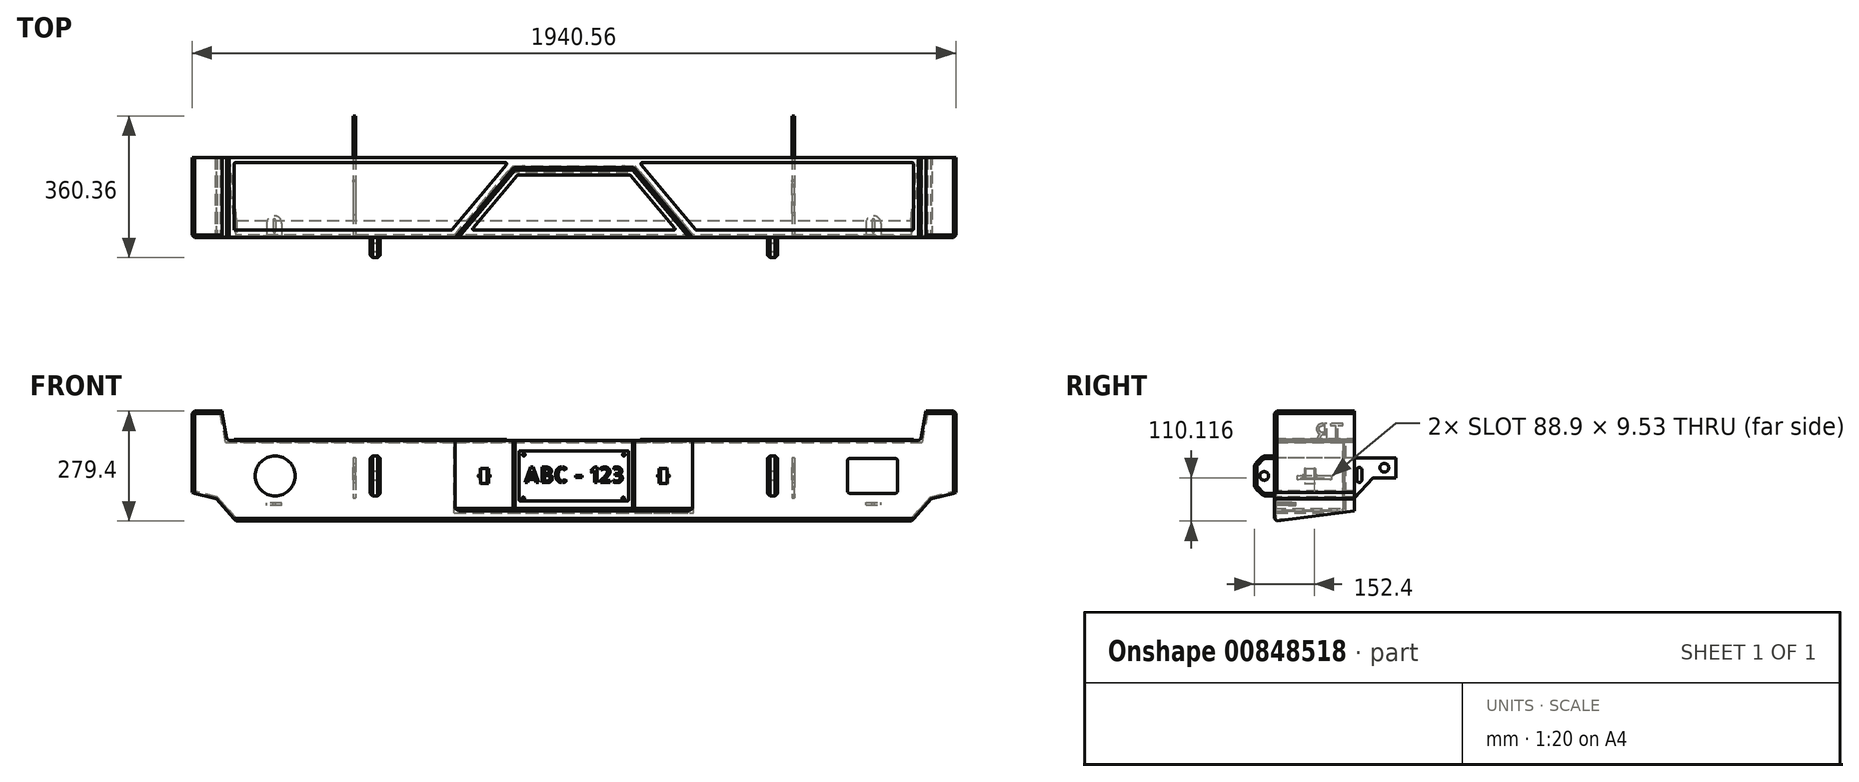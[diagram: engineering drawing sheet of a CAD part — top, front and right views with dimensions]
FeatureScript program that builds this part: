
annotation { "Feature Type Name" : "Feature", "Feature Type Description" : "" }
export const myFeature = defineFeature(function(context is Context, id is Id, definition is map)
    precondition{}
    {
        {
            var Q0;
            Q0=qCreatedBy(makeId("Top.planeOp"),FACE);
            var sketch = newSketch(context, id + "F0", { "sketchPlane" : qUnion([Q0])});
            skLineSegment(sketch, "E0.bottom", {"start": v(-970.28, -101.6) * mm, "end": v(970.28, -101.6) * mm});
            skLineSegment(sketch, "E0.top", {"start": v(-970.28, 101.6) * mm, "end": v(970.28, 101.6) * mm});
            skLineSegment(sketch, "E0.left", {"start": v(-970.28, -101.6) * mm, "end": v(-970.28, 101.6) * mm});
            skLineSegment(sketch, "E0.right", {"start": v(970.28, -101.6) * mm, "end": v(970.28, 101.6) * mm});
            skPoint(sketch, "E0.middle", {"position": v(0, 0) * mm});
            skSolve(sketch);
        }
        {
            var Q0;
            Q0=qSketchRegion(id+"F0",true);
            extrude(context, id + "F1", {"entities" : qUnion([Q0]), "depth" : 279.4 * mm, "offsetDistance" : 25.4 * mm});
        }
        {
            var Q0;
            Q0=makeQuery(id+"F1.opExtrude","SWEPT_FACE",FACE,{"disambiguationData":[OSD([sQuery(id+"F0.wireOp",EDGE,"E0.bottom")])]});
            var sketch = newSketch(context, id + "F2", { "sketchPlane" : qUnion([Q0])});
            skLineSegment(sketch, "E1", {"start": v(-970.28, 72.27) * mm, "end": v(-908.72, 57.25) * mm});
            skLineSegment(sketch, "E2", {"start": v(-908.72, 57.25) * mm, "end": v(-858.44, 0) * mm});
            skLineSegment(sketch, "E3.MirrorCS", {"start": v(908.72, 57.25) * mm, "end": v(858.44, 0) * mm});
            skLineSegment(sketch, "E4.MirrorCS", {"start": v(970.28, 72.27) * mm, "end": v(908.72, 57.25) * mm});
            skSolve(sketch);
        }
        {
            var Q0;
            {var subQ0=sQuery(id+"F2.wireOp",EDGE,"E1");Q0=makeQuery(id+"F2.imprint","IMPRINT",FACE,{"disambiguationData":[TD([[makeQuery(id+"F2.imprint","IMPRINT",EDGE,{"derivedFrom":subQ0}),-1.0]])]});}
            var Q1;
            {var subQ0=sQuery(id+"F2.wireOp",EDGE,"E3.MirrorCS");Q1=makeQuery(id+"F2.imprint","IMPRINT",FACE,{"disambiguationData":[TD([[makeQuery(id+"F2.imprint","IMPRINT",EDGE,{"derivedFrom":subQ0}),1.0]])]});}
            extrude(context, id + "F3", {"entities" : qUnion([Q0, Q1]), "operationType" : NewBodyOperationType.REMOVE, "endBound" : BoundingType.THROUGH_ALL, "oppositeDirection" : true, "depth" : 25.4 * mm});
        }
        {
            var Q0;
            Q0=makeQuery(id+"F1.opExtrude","SWEPT_FACE",FACE,{"disambiguationData":[OSD([sQuery(id+"F0.wireOp",EDGE,"E0.bottom")])]});
            var sketch = newSketch(context, id + "F4", { "sketchPlane" : qUnion([Q0])});
            skLineSegment(sketch, "E5", {"start": v(-970.28, 279.4) * mm, "end": v(-894.08, 279.4) * mm});
            skLineSegment(sketch, "E6", {"start": v(-894.08, 279.4) * mm, "end": v(-880.85, 204.36) * mm});
            skLineSegment(sketch, "E7", {"start": v(-880.85, 204.36) * mm, "end": v(880.85, 204.36) * mm});
            skLineSegment(sketch, "E8", {"start": v(880.85, 204.36) * mm, "end": v(894.08, 279.4) * mm});
            skLineSegment(sketch, "E9", {"start": v(894.08, 279.4) * mm, "end": v(970.28, 279.4) * mm});
            skSolve(sketch);
        }
        {
            var Q0;
            {var subQ0=sQuery(id+"F4.wireOp",EDGE,"E6");Q0=makeQuery(id+"F4.imprint","IMPRINT",FACE,{"disambiguationData":[TD([[makeQuery(id+"F4.imprint","IMPRINT",EDGE,{"derivedFrom":subQ0}),1.0]])]});}
            extrude(context, id + "F5", {"entities" : qUnion([Q0]), "operationType" : NewBodyOperationType.REMOVE, "endBound" : BoundingType.THROUGH_ALL, "oppositeDirection" : true, "depth" : 25.4 * mm});
        }
        {
            var Q0;
            Q0=makeQuery(id+"F5.boolean.opBoolean","COPY",FACE,{"derivedFrom":makeQuery(id+"F5.opExtrude","SWEPT_FACE",FACE,{"disambiguationData":[OSD([sQuery(id+"F4.wireOp",EDGE,"E7")])]})});
            var sketch = newSketch(context, id + "F6", { "sketchPlane" : qUnion([Q0])});
            skLineSegment(sketch, "E10", {"start": v(-301.6, -101.6) * mm, "end": v(-152.4, 76.2) * mm});
            skLineSegment(sketch, "E11", {"start": v(-152.4, 76.2) * mm, "end": v(152.4, 76.2) * mm});
            skLineSegment(sketch, "E12", {"start": v(152.4, 76.2) * mm, "end": v(301.6, -101.6) * mm});
            skSolve(sketch);
        }
        {
            var Q0;
            {var subQ0=sQuery(id+"F6.wireOp",EDGE,"E10");Q0=makeQuery(id+"F6.imprint","IMPRINT",FACE,{"disambiguationData":[TD([[makeQuery(id+"F6.imprint","IMPRINT",EDGE,{"derivedFrom":subQ0}),-1.0]])]});}
            extrude(context, id + "F7", {"entities" : qUnion([Q0]), "operationType" : NewBodyOperationType.REMOVE, "oppositeDirection" : true, "depth" : 178.96 * mm});
        }
        {
            var Q0;
            Q0=makeQuery(id+"F1.opExtrude","SWEPT_FACE",FACE,{"disambiguationData":[OSD([sQuery(id+"F0.wireOp",EDGE,"E0.bottom")])]});
            var sketch = newSketch(context, id + "F8", { "sketchPlane" : qUnion([Q0])});
            skLineSegment(sketch, "E13.bottom", {"start": v(-492.1, 165.68) * mm, "end": v(-517.5, 165.68) * mm});
            skLineSegment(sketch, "E13.top", {"start": v(-492.1, 64.08) * mm, "end": v(-517.5, 64.08) * mm});
            skLineSegment(sketch, "E13.left", {"start": v(-492.1, 165.68) * mm, "end": v(-492.1, 64.08) * mm});
            skLineSegment(sketch, "E13.right", {"start": v(-517.5, 165.68) * mm, "end": v(-517.5, 64.08) * mm});
            skPoint(sketch, "E13.middle", {"position": v(-504.8, 114.88) * mm});
            skPoint(sketch, "E13.middle.positionSnap0", {"position": v(-301.6, 114.88) * mm});
            skPoint(sketch, "E13.centerSnap0", {"position": v(-301.6, 114.88) * mm});
            skLineSegment(sketch, "E14.bottom", {"start": v(492.1, 165.68) * mm, "end": v(517.5, 165.68) * mm});
            skLineSegment(sketch, "E14.top", {"start": v(492.1, 64.08) * mm, "end": v(517.5, 64.08) * mm});
            skLineSegment(sketch, "E14.left", {"start": v(492.1, 165.68) * mm, "end": v(492.1, 64.08) * mm});
            skLineSegment(sketch, "E14.right", {"start": v(517.5, 165.68) * mm, "end": v(517.5, 64.08) * mm});
            skPoint(sketch, "E14.middle", {"position": v(504.8, 114.88) * mm});
            skPoint(sketch, "E14.middle.positionSnap0", {"position": v(301.6, 114.88) * mm});
            skPoint(sketch, "E14.centerSnap0", {"position": v(301.6, 114.88) * mm});
            skSolve(sketch);
        }
        {
            var Q0;
            Q0=qSketchRegion(id+"F8",true);
            extrude(context, id + "F9", {"entities" : qUnion([Q0]), "depth" : 50.8 * mm});
        }
        {
            var Q0;
            Q0=makeQuery(id+"F9.opExtrude","SWEPT_FACE",FACE,{"disambiguationData":[OSD([sQuery(id+"F8.wireOp",EDGE,"E13.right")])]});
            var sketch = newSketch(context, id + "F10", { "sketchPlane" : qUnion([Q0])});
            skCircle(sketch, "E15", {"center": v(127, 114.88) * mm, "radius": 11.11 * mm});
            skPoint(sketch, "E15.centerSnap0", {"position": v(127, 165.68) * mm});
            skPoint(sketch, "E15.centerSnap1", {"position": v(152.4, 114.88) * mm});
            skSolve(sketch);
        }
        {
            var Q0;
            Q0=qSketchRegion(id+"F10",true);
            extrude(context, id + "F11", {"entities" : qUnion([Q0]), "operationType" : NewBodyOperationType.REMOVE, "endBound" : BoundingType.THROUGH_ALL, "oppositeDirection" : true, "depth" : 25.4 * mm});
        }
        {
            var Q0;
            Q0=makeQuery(id+"F9.opExtrude","CAP_EDGE",EDGE,{"disambiguationData":[OSD([sQuery(id+"F8.wireOp",EDGE,"E13.bottom")])],"isStart":false});
            var Q1;
            Q1=makeQuery(id+"F9.opExtrude","CAP_EDGE",EDGE,{"disambiguationData":[OSD([sQuery(id+"F8.wireOp",EDGE,"E13.top")])],"isStart":false});
            var Q2;
            Q2=makeQuery(id+"F9.opExtrude","CAP_EDGE",EDGE,{"disambiguationData":[OSD([sQuery(id+"F8.wireOp",EDGE,"E14.bottom")])],"isStart":false});
            var Q3;
            Q3=makeQuery(id+"F9.opExtrude","CAP_EDGE",EDGE,{"disambiguationData":[OSD([sQuery(id+"F8.wireOp",EDGE,"E14.top")])],"isStart":false});
            chamfer(context, id + "F12", {"entities" : qUnion([Q0, Q1, Q2, Q3]), "width" : 22.22 * mm, "tangentPropagation" : true});
        }
        {
            var Q0;
            {var subQ0=sQuery(id+"F8.wireOp",EDGE,"E13.bottom");Q0=makeQuery(id+"F12.opChamfer","BLEND_EDGE",EDGE,{"blendedFrom":[makeQuery(id+"F9.opExtrude","CAP_EDGE",EDGE,{"disambiguationData":[OSD([subQ0])],"isStart":false}),makeQuery(id+"F9.opExtrude","SWEPT_FACE",FACE,{"disambiguationData":[OSD([subQ0])]})],"blendedInto":[makeQuery(id+"F9.opExtrude","SWEPT_FACE",FACE,{"disambiguationData":[OSD([subQ0])]})]});}
            var Q1;
            {var subQ0=sQuery(id+"F8.wireOp",EDGE,"E13.bottom");Q1=makeQuery(id+"F12.opChamfer","BLEND_EDGE",EDGE,{"blendedFrom":[makeQuery(id+"F9.opExtrude","CAP_EDGE",EDGE,{"disambiguationData":[OSD([subQ0])],"isStart":false}),makeQuery(id+"F9.opExtrude","CAP_FACE",FACE,{"disambiguationData":[OSD([subQ0,sQuery(id+"F8.wireOp",EDGE,"E13.top"),sQuery(id+"F8.wireOp",EDGE,"E13.left"),sQuery(id+"F8.wireOp",EDGE,"E13.right")])],"isStart":false})],"blendedInto":[makeQuery(id+"F9.opExtrude","CAP_FACE",FACE,{"disambiguationData":[OSD([subQ0,sQuery(id+"F8.wireOp",EDGE,"E13.top"),sQuery(id+"F8.wireOp",EDGE,"E13.left"),sQuery(id+"F8.wireOp",EDGE,"E13.right")])],"isStart":false})]});}
            var Q2;
            {var subQ0=sQuery(id+"F8.wireOp",EDGE,"E13.top");Q2=makeQuery(id+"F12.opChamfer","BLEND_EDGE",EDGE,{"blendedFrom":[makeQuery(id+"F9.opExtrude","CAP_EDGE",EDGE,{"disambiguationData":[OSD([subQ0])],"isStart":false}),makeQuery(id+"F9.opExtrude","CAP_FACE",FACE,{"disambiguationData":[OSD([sQuery(id+"F8.wireOp",EDGE,"E13.bottom"),subQ0,sQuery(id+"F8.wireOp",EDGE,"E13.left"),sQuery(id+"F8.wireOp",EDGE,"E13.right")])],"isStart":false})],"blendedInto":[makeQuery(id+"F9.opExtrude","CAP_FACE",FACE,{"disambiguationData":[OSD([sQuery(id+"F8.wireOp",EDGE,"E13.bottom"),subQ0,sQuery(id+"F8.wireOp",EDGE,"E13.left"),sQuery(id+"F8.wireOp",EDGE,"E13.right")])],"isStart":false})]});}
            var Q3;
            {var subQ0=sQuery(id+"F8.wireOp",EDGE,"E13.top");Q3=makeQuery(id+"F12.opChamfer","BLEND_EDGE",EDGE,{"blendedFrom":[makeQuery(id+"F9.opExtrude","CAP_EDGE",EDGE,{"disambiguationData":[OSD([subQ0])],"isStart":false}),makeQuery(id+"F9.opExtrude","SWEPT_FACE",FACE,{"disambiguationData":[OSD([subQ0])]})],"blendedInto":[makeQuery(id+"F9.opExtrude","SWEPT_FACE",FACE,{"disambiguationData":[OSD([subQ0])]})]});}
            var Q4;
            {var subQ0=sQuery(id+"F8.wireOp",EDGE,"E14.bottom");Q4=makeQuery(id+"F12.opChamfer","BLEND_EDGE",EDGE,{"blendedFrom":[makeQuery(id+"F9.opExtrude","CAP_EDGE",EDGE,{"disambiguationData":[OSD([subQ0])],"isStart":false}),makeQuery(id+"F9.opExtrude","SWEPT_FACE",FACE,{"disambiguationData":[OSD([subQ0])]})],"blendedInto":[makeQuery(id+"F9.opExtrude","SWEPT_FACE",FACE,{"disambiguationData":[OSD([subQ0])]})]});}
            var Q5;
            {var subQ0=sQuery(id+"F8.wireOp",EDGE,"E14.bottom");Q5=makeQuery(id+"F12.opChamfer","BLEND_EDGE",EDGE,{"blendedFrom":[makeQuery(id+"F9.opExtrude","CAP_EDGE",EDGE,{"disambiguationData":[OSD([subQ0])],"isStart":false}),makeQuery(id+"F9.opExtrude","CAP_FACE",FACE,{"disambiguationData":[OSD([subQ0,sQuery(id+"F8.wireOp",EDGE,"E14.top"),sQuery(id+"F8.wireOp",EDGE,"E14.left"),sQuery(id+"F8.wireOp",EDGE,"E14.right")])],"isStart":false})],"blendedInto":[makeQuery(id+"F9.opExtrude","CAP_FACE",FACE,{"disambiguationData":[OSD([subQ0,sQuery(id+"F8.wireOp",EDGE,"E14.top"),sQuery(id+"F8.wireOp",EDGE,"E14.left"),sQuery(id+"F8.wireOp",EDGE,"E14.right")])],"isStart":false})]});}
            var Q6;
            {var subQ0=sQuery(id+"F8.wireOp",EDGE,"E14.top");Q6=makeQuery(id+"F12.opChamfer","BLEND_EDGE",EDGE,{"blendedFrom":[makeQuery(id+"F9.opExtrude","CAP_EDGE",EDGE,{"disambiguationData":[OSD([subQ0])],"isStart":false}),makeQuery(id+"F9.opExtrude","CAP_FACE",FACE,{"disambiguationData":[OSD([sQuery(id+"F8.wireOp",EDGE,"E14.bottom"),subQ0,sQuery(id+"F8.wireOp",EDGE,"E14.left"),sQuery(id+"F8.wireOp",EDGE,"E14.right")])],"isStart":false})],"blendedInto":[makeQuery(id+"F9.opExtrude","CAP_FACE",FACE,{"disambiguationData":[OSD([sQuery(id+"F8.wireOp",EDGE,"E14.bottom"),subQ0,sQuery(id+"F8.wireOp",EDGE,"E14.left"),sQuery(id+"F8.wireOp",EDGE,"E14.right")])],"isStart":false})]});}
            var Q7;
            {var subQ0=sQuery(id+"F8.wireOp",EDGE,"E14.top");Q7=makeQuery(id+"F12.opChamfer","BLEND_EDGE",EDGE,{"blendedFrom":[makeQuery(id+"F9.opExtrude","CAP_EDGE",EDGE,{"disambiguationData":[OSD([subQ0])],"isStart":false}),makeQuery(id+"F9.opExtrude","SWEPT_FACE",FACE,{"disambiguationData":[OSD([subQ0])]})],"blendedInto":[makeQuery(id+"F9.opExtrude","SWEPT_FACE",FACE,{"disambiguationData":[OSD([subQ0])]})]});}
            fillet(context, id + "F13", {"entities" : qUnion([Q0, Q1, Q2, Q3, Q4, Q5, Q6, Q7]), "radius" : 19.05 * mm, "tangentPropagation" : true, "allowEdgeOverflow" : false});
        }
        {
            var Q0;
            Q0=makeQuery(id+"F9.opExtrude","SWEPT_EDGE",EDGE,{"disambiguationData":[OSD([sQuery(id+"F8.wireOp",EDGE,"E13.bottom"),sQuery(id+"F8.wireOp",EDGE,"E13.right")])]});
            var Q1;
            Q1=makeQuery(id+"F9.opExtrude","SWEPT_EDGE",EDGE,{"disambiguationData":[OSD([sQuery(id+"F8.wireOp",EDGE,"E13.bottom"),sQuery(id+"F8.wireOp",EDGE,"E13.left")])]});
            var Q2;
            Q2=makeQuery(id+"F9.opExtrude","SWEPT_EDGE",EDGE,{"disambiguationData":[OSD([sQuery(id+"F8.wireOp",EDGE,"E14.bottom"),sQuery(id+"F8.wireOp",EDGE,"E14.left")])]});
            var Q3;
            Q3=makeQuery(id+"F9.opExtrude","SWEPT_EDGE",EDGE,{"disambiguationData":[OSD([sQuery(id+"F8.wireOp",EDGE,"E14.bottom"),sQuery(id+"F8.wireOp",EDGE,"E14.right")])]});
            chamfer(context, id + "F14", {"entities" : qUnion([Q0, Q1, Q2, Q3]), "width" : 6.35 * mm, "tangentPropagation" : true});
        }
        {
            var Q0;
            Q0=makeQuery(id+"F1.opExtrude","SWEPT_FACE",FACE,{"disambiguationData":[OSD([sQuery(id+"F0.wireOp",EDGE,"E0.top")])]});
            shell(context, id + "F15", {"entities" : qUnion([Q0]), "thickness" : 4.76 * mm});
        }
        {
            var Q0;
            Q0=makeQuery(id+"F1.opExtrude","SWEPT_FACE",FACE,{"disambiguationData":[OSD([sQuery(id+"F0.wireOp",EDGE,"E0.bottom")])]});
            var sketch = newSketch(context, id + "F16", { "sketchPlane" : qUnion([Q0])});
            skCircle(sketch, "E16", {"center": v(-758.8, 114.88) * mm, "radius": 50.8 * mm});
            skPoint(sketch, "E16.centerSnap0", {"position": v(-301.6, 114.88) * mm});
            skPoint(sketch, "E17.centerSnap0", {"position": v(301.6, 114.88) * mm});
            skLineSegment(sketch, "E18.bottom", {"start": v(695.3, 70.43) * mm, "end": v(822.3, 70.43) * mm});
            skLineSegment(sketch, "E18.top", {"start": v(695.3, 159.33) * mm, "end": v(822.3, 159.33) * mm});
            skLineSegment(sketch, "E18.left", {"start": v(695.3, 70.43) * mm, "end": v(695.3, 159.33) * mm});
            skLineSegment(sketch, "E18.right", {"start": v(822.3, 70.43) * mm, "end": v(822.3, 159.33) * mm});
            skPoint(sketch, "E18.middle", {"position": v(758.8, 114.88) * mm});
            skSolve(sketch);
        }
        {
            var Q0;
            Q0=qSketchRegion(id+"F16",true);
            extrude(context, id + "F17", {"entities" : qUnion([Q0]), "operationType" : NewBodyOperationType.REMOVE, "endBound" : BoundingType.THROUGH_ALL, "oppositeDirection" : true, "depth" : 25.4 * mm});
        }
        {
            var Q0;
            Q0=makeQuery(id+"F1.opExtrude","CAP_EDGE",EDGE,{"disambiguationData":[OSD([sQuery(id+"F0.wireOp",EDGE,"E0.bottom")])],"isStart":true});
            var Q1;
            Q1=makeQuery(id+"F3.boolean.opBoolean","COPY",EDGE,{"derivedFrom":makeQuery(id+"F3.opExtrude","CAP_EDGE",EDGE,{"disambiguationData":[OSD([sQuery(id+"F2.wireOp",EDGE,"E2")])],"isStart":true})});
            var Q2;
            Q2=makeQuery(id+"F3.boolean.opBoolean","COPY",EDGE,{"derivedFrom":makeQuery(id+"F3.opExtrude","CAP_EDGE",EDGE,{"disambiguationData":[OSD([sQuery(id+"F2.wireOp",EDGE,"E1")])],"isStart":true})});
            var Q3;
            Q3=makeQuery(id+"F3.boolean.opBoolean","COPY",EDGE,{"derivedFrom":makeQuery(id+"F3.opExtrude","CAP_EDGE",EDGE,{"disambiguationData":[OSD([sQuery(id+"F2.wireOp",EDGE,"E3.MirrorCS")])],"isStart":true})});
            var Q4;
            Q4=makeQuery(id+"F3.boolean.opBoolean","COPY",EDGE,{"derivedFrom":makeQuery(id+"F3.opExtrude","CAP_EDGE",EDGE,{"disambiguationData":[OSD([sQuery(id+"F2.wireOp",EDGE,"E4.MirrorCS")])],"isStart":true})});
            var Q5;
            Q5=makeQuery(id+"F1.opExtrude","SWEPT_EDGE",EDGE,{"disambiguationData":[OSD([sQuery(id+"F0.wireOp",EDGE,"E0.bottom"),sQuery(id+"F0.wireOp",EDGE,"E0.right")])]});
            var Q6;
            Q6=makeQuery(id+"F1.opExtrude","SWEPT_EDGE",EDGE,{"disambiguationData":[OSD([sQuery(id+"F0.wireOp",EDGE,"E0.bottom"),sQuery(id+"F0.wireOp",EDGE,"E0.left")])]});
            var Q7;
            Q7=makeQuery(id+"F3.boolean.opBoolean","COPY",EDGE,{"derivedFrom":makeQuery(id+"F3.opExtrude","SWEPT_EDGE",EDGE,{"disambiguationData":[OSD([sQuery(id+"F0.wireOp",EDGE,"E0.bottom"),sQuery(id+"F0.wireOp",EDGE,"E0.left"),sQuery(id+"F2.wireOp",EDGE,"E1")])]})});
            var Q8;
            Q8=makeQuery(id+"F3.boolean.opBoolean","COPY",EDGE,{"derivedFrom":makeQuery(id+"F3.opExtrude","SWEPT_EDGE",EDGE,{"disambiguationData":[OSD([sQuery(id+"F2.wireOp",EDGE,"E1"),sQuery(id+"F2.wireOp",EDGE,"E2")])]})});
            var Q9;
            Q9=makeQuery(id+"F3.boolean.opBoolean","COPY",EDGE,{"derivedFrom":makeQuery(id+"F3.opExtrude","SWEPT_EDGE",EDGE,{"disambiguationData":[OSD([sQuery(id+"F0.wireOp",EDGE,"E0.bottom"),sQuery(id+"F2.wireOp",EDGE,"E2")])]})});
            var Q10;
            Q10=makeQuery(id+"F3.boolean.opBoolean","COPY",EDGE,{"derivedFrom":makeQuery(id+"F3.opExtrude","SWEPT_EDGE",EDGE,{"disambiguationData":[OSD([sQuery(id+"F0.wireOp",EDGE,"E0.bottom"),sQuery(id+"F2.wireOp",EDGE,"E3.MirrorCS")])]})});
            var Q11;
            Q11=makeQuery(id+"F3.boolean.opBoolean","COPY",EDGE,{"derivedFrom":makeQuery(id+"F3.opExtrude","SWEPT_EDGE",EDGE,{"disambiguationData":[OSD([sQuery(id+"F2.wireOp",EDGE,"E3.MirrorCS"),sQuery(id+"F2.wireOp",EDGE,"E4.MirrorCS")])]})});
            var Q12;
            Q12=makeQuery(id+"F3.boolean.opBoolean","COPY",EDGE,{"derivedFrom":makeQuery(id+"F3.opExtrude","SWEPT_EDGE",EDGE,{"disambiguationData":[OSD([sQuery(id+"F0.wireOp",EDGE,"E0.bottom"),sQuery(id+"F0.wireOp",EDGE,"E0.right"),sQuery(id+"F2.wireOp",EDGE,"E4.MirrorCS")])]})});
            var Q13;
            Q13=makeQuery(id+"F1.opExtrude","CAP_EDGE",EDGE,{"disambiguationData":[OSD([sQuery(id+"F0.wireOp",EDGE,"E0.left")])],"isStart":false});
            var Q14;
            Q14=makeQuery(id+"F1.opExtrude","CAP_EDGE",EDGE,{"disambiguationData":[OSD([sQuery(id+"F0.wireOp",EDGE,"E0.right")])],"isStart":false});
            var Q15;
            {var subQ0=sQuery(id+"F0.wireOp",EDGE,"E0.bottom");var subQ1=sQuery(id+"F0.wireOp",EDGE,"E0.right");Q15=makeQuery(id+"F5.boolean.opBoolean","SPLIT",EDGE,{"disambiguationData":[TD([makeQuery(id+"F1.opExtrude","SWEPT_FACE",FACE,{"disambiguationData":[OSD([subQ1])]})])],"derivedFrom":makeQuery(id+"F1.opExtrude","CAP_EDGE",EDGE,{"disambiguationData":[OSD([subQ0])],"isStart":false})});}
            var Q16;
            Q16=makeQuery(id+"F5.boolean.opBoolean","COPY",EDGE,{"derivedFrom":makeQuery(id+"F5.opExtrude","CAP_EDGE",EDGE,{"disambiguationData":[OSD([sQuery(id+"F4.wireOp",EDGE,"E8")])],"isStart":true})});
            var Q17;
            {var subQ0=sQuery(id+"F4.wireOp",EDGE,"E7");Q17=makeQuery(id+"F7.boolean.opBoolean","SPLIT",EDGE,{"disambiguationData":[TD([makeQuery(id+"F5.boolean.opBoolean","COPY",FACE,{"derivedFrom":makeQuery(id+"F5.opExtrude","SWEPT_FACE",FACE,{"disambiguationData":[OSD([sQuery(id+"F4.wireOp",EDGE,"E8")])]})})])],"derivedFrom":makeQuery(id+"F5.boolean.opBoolean","COPY",EDGE,{"derivedFrom":makeQuery(id+"F5.opExtrude","CAP_EDGE",EDGE,{"disambiguationData":[OSD([subQ0])],"isStart":true})})});}
            var Q18;
            {var subQ0=sQuery(id+"F4.wireOp",EDGE,"E7");Q18=makeQuery(id+"F7.boolean.opBoolean","SPLIT",EDGE,{"disambiguationData":[TD([makeQuery(id+"F5.boolean.opBoolean","COPY",FACE,{"derivedFrom":makeQuery(id+"F5.opExtrude","SWEPT_FACE",FACE,{"disambiguationData":[OSD([sQuery(id+"F4.wireOp",EDGE,"E6")])]})})])],"derivedFrom":makeQuery(id+"F5.boolean.opBoolean","COPY",EDGE,{"derivedFrom":makeQuery(id+"F5.opExtrude","CAP_EDGE",EDGE,{"disambiguationData":[OSD([subQ0])],"isStart":true})})});}
            var Q19;
            {var subQ0=sQuery(id+"F0.wireOp",EDGE,"E0.bottom");var subQ1=sQuery(id+"F0.wireOp",EDGE,"E0.left");Q19=makeQuery(id+"F5.boolean.opBoolean","SPLIT",EDGE,{"disambiguationData":[TD([makeQuery(id+"F1.opExtrude","SWEPT_FACE",FACE,{"disambiguationData":[OSD([subQ1])]})])],"derivedFrom":makeQuery(id+"F1.opExtrude","CAP_EDGE",EDGE,{"disambiguationData":[OSD([subQ0])],"isStart":false})});}
            var Q20;
            Q20=makeQuery(id+"F5.boolean.opBoolean","COPY",EDGE,{"derivedFrom":makeQuery(id+"F5.opExtrude","CAP_EDGE",EDGE,{"disambiguationData":[OSD([sQuery(id+"F4.wireOp",EDGE,"E6")])],"isStart":true})});
            var Q21;
            Q21=makeQuery(id+"F5.boolean.opBoolean","COPY",EDGE,{"derivedFrom":makeQuery(id+"F5.opExtrude","SWEPT_EDGE",EDGE,{"disambiguationData":[OSD([sQuery(id+"F0.wireOp",EDGE,"E0.bottom"),sQuery(id+"F4.wireOp",EDGE,"E5"),sQuery(id+"F4.wireOp",EDGE,"E6")])]})});
            var Q22;
            Q22=makeQuery(id+"F5.boolean.opBoolean","COPY",EDGE,{"derivedFrom":makeQuery(id+"F5.opExtrude","SWEPT_EDGE",EDGE,{"disambiguationData":[OSD([sQuery(id+"F0.wireOp",EDGE,"E0.bottom"),sQuery(id+"F4.wireOp",EDGE,"E8"),sQuery(id+"F4.wireOp",EDGE,"E9")])]})});
            var Q23;
            Q23=makeQuery(id+"F5.boolean.opBoolean","COPY",EDGE,{"derivedFrom":makeQuery(id+"F5.opExtrude","SWEPT_EDGE",EDGE,{"disambiguationData":[OSD([sQuery(id+"F4.wireOp",EDGE,"E7"),sQuery(id+"F4.wireOp",EDGE,"E8")])]})});
            var Q24;
            Q24=makeQuery(id+"F5.boolean.opBoolean","COPY",EDGE,{"derivedFrom":makeQuery(id+"F5.opExtrude","SWEPT_EDGE",EDGE,{"disambiguationData":[OSD([sQuery(id+"F4.wireOp",EDGE,"E6"),sQuery(id+"F4.wireOp",EDGE,"E7")])]})});
            var Q25;
            Q25=makeQuery(id+"F7.boolean.opBoolean","COPY",EDGE,{"derivedFrom":makeQuery(id+"F7.opExtrude","CAP_EDGE",EDGE,{"disambiguationData":[OSD([sQuery(id+"F6.wireOp",EDGE,"E10")])],"isStart":true})});
            var Q26;
            Q26=makeQuery(id+"F7.boolean.opBoolean","COPY",EDGE,{"derivedFrom":makeQuery(id+"F7.opExtrude","SWEPT_EDGE",EDGE,{"disambiguationData":[OSD([sQuery(id+"F4.wireOp",EDGE,"E7"),sQuery(id+"F6.wireOp",EDGE,"E10")])]})});
            var Q27;
            Q27=makeQuery(id+"F7.boolean.opBoolean","COPY",EDGE,{"derivedFrom":makeQuery(id+"F7.opExtrude","CAP_EDGE",EDGE,{"disambiguationData":[OSD([sQuery(id+"F4.wireOp",EDGE,"E7")])],"isStart":false})});
            var Q28;
            Q28=makeQuery(id+"F7.boolean.opBoolean","COPY",EDGE,{"derivedFrom":makeQuery(id+"F7.opExtrude","SWEPT_EDGE",EDGE,{"disambiguationData":[OSD([sQuery(id+"F4.wireOp",EDGE,"E7"),sQuery(id+"F6.wireOp",EDGE,"E12")])]})});
            var Q29;
            Q29=makeQuery(id+"F7.boolean.opBoolean","COPY",EDGE,{"derivedFrom":makeQuery(id+"F7.opExtrude","CAP_EDGE",EDGE,{"disambiguationData":[OSD([sQuery(id+"F6.wireOp",EDGE,"E12")])],"isStart":true})});
            var Q30;
            Q30=makeQuery(id+"F7.boolean.opBoolean","COPY",EDGE,{"derivedFrom":makeQuery(id+"F7.opExtrude","CAP_EDGE",EDGE,{"disambiguationData":[OSD([sQuery(id+"F6.wireOp",EDGE,"E11")])],"isStart":true})});
            var Q31;
            Q31=makeQuery(id+"F7.boolean.opBoolean","COPY",EDGE,{"derivedFrom":makeQuery(id+"F7.opExtrude","SWEPT_EDGE",EDGE,{"disambiguationData":[OSD([sQuery(id+"F6.wireOp",EDGE,"E11"),sQuery(id+"F6.wireOp",EDGE,"E12")])]})});
            var Q32;
            Q32=makeQuery(id+"F7.boolean.opBoolean","COPY",EDGE,{"derivedFrom":makeQuery(id+"F7.opExtrude","SWEPT_EDGE",EDGE,{"disambiguationData":[OSD([sQuery(id+"F6.wireOp",EDGE,"E10"),sQuery(id+"F6.wireOp",EDGE,"E11")])]})});
            var Q33;
            Q33=makeQuery(id+"F7.boolean.opBoolean","COPY",EDGE,{"derivedFrom":makeQuery(id+"F7.opExtrude","CAP_EDGE",EDGE,{"disambiguationData":[OSD([sQuery(id+"F6.wireOp",EDGE,"E10")])],"isStart":false})});
            var Q34;
            Q34=makeQuery(id+"F7.boolean.opBoolean","COPY",EDGE,{"derivedFrom":makeQuery(id+"F7.opExtrude","CAP_EDGE",EDGE,{"disambiguationData":[OSD([sQuery(id+"F6.wireOp",EDGE,"E11")])],"isStart":false})});
            var Q35;
            Q35=makeQuery(id+"F7.boolean.opBoolean","COPY",EDGE,{"derivedFrom":makeQuery(id+"F7.opExtrude","CAP_EDGE",EDGE,{"disambiguationData":[OSD([sQuery(id+"F6.wireOp",EDGE,"E12")])],"isStart":false})});
            chamfer(context, id + "F18", {"entities" : qUnion([Q0, Q1, Q2, Q3, Q4, Q5, Q6, Q7, Q8, Q9, Q10, Q11, Q12, Q13, Q14, Q15, Q16, Q17, Q18, Q19, Q20, Q21, Q22, Q23, Q24, Q25, Q26, Q27, Q28, Q29, Q30, Q31, Q32, Q33, Q34, Q35]), "width" : 6.35 * mm, "tangentPropagation" : true});
        }
        {
            var Q0;
            Q0=makeQuery(id+"F15.opShell","OFFSET_FACE",FACE,{"disambiguationData":[OSD([sQuery(id+"F0.wireOp",EDGE,"E0.bottom")])]});
            var sketch = newSketch(context, id + "F19", { "sketchPlane" : qUnion([Q0])});
            skLineSegment(sketch, "E19.bottom", {"start": v(-741.96, 40.86) * mm, "end": v(-780.06, 40.86) * mm});
            skLineSegment(sketch, "E19.top", {"start": v(-741.96, 47.2) * mm, "end": v(-780.06, 47.2) * mm});
            skLineSegment(sketch, "E19.left", {"start": v(-741.96, 40.86) * mm, "end": v(-741.96, 47.2) * mm});
            skLineSegment(sketch, "E19.right", {"start": v(-780.06, 40.86) * mm, "end": v(-780.06, 47.2) * mm});
            skPoint(sketch, "E19.middle", {"position": v(-761.01, 44.03) * mm});
            skLineSegment(sketch, "E20.bottom", {"start": v(741.96, 40.36) * mm, "end": v(780.06, 40.36) * mm});
            skLineSegment(sketch, "E20.top", {"start": v(741.96, 46.71) * mm, "end": v(780.06, 46.71) * mm});
            skLineSegment(sketch, "E20.left", {"start": v(741.96, 40.36) * mm, "end": v(741.96, 46.71) * mm});
            skLineSegment(sketch, "E20.right", {"start": v(780.06, 40.36) * mm, "end": v(780.06, 46.71) * mm});
            skPoint(sketch, "E20.middle", {"position": v(761.01, 43.54) * mm});
            skSolve(sketch);
        }
        {
            var Q0;
            Q0=qSketchRegion(id+"F19",true);
            extrude(context, id + "F20", {"entities" : qUnion([Q0]), "depth" : 50.8 * mm});
        }
        {
            var Q0;
            Q0=makeQuery(id+"F20.opExtrude","SWEPT_FACE",FACE,{"disambiguationData":[OSD([sQuery(id+"F19.wireOp",EDGE,"E19.top")])]});
            var sketch = newSketch(context, id + "F21", { "sketchPlane" : qUnion([Q0])});
            skLineSegment(sketch, "E21.bottom", {"start": v(757.84, -53.98) * mm, "end": v(764.19, -53.98) * mm});
            skLineSegment(sketch, "E21.top", {"start": v(757.84, -88.9) * mm, "end": v(764.19, -88.9) * mm});
            skLineSegment(sketch, "E21.left", {"start": v(757.84, -53.98) * mm, "end": v(757.84, -88.9) * mm});
            skLineSegment(sketch, "E21.right", {"start": v(764.19, -53.98) * mm, "end": v(764.19, -88.9) * mm});
            skPoint(sketch, "E21.middle", {"position": v(761.01, -71.44) * mm});
            skPoint(sketch, "E21.middle.positionSnap0", {"position": v(761.01, -96.84) * mm});
            skPoint(sketch, "E21.middle.positionSnap1", {"position": v(741.96, -71.44) * mm});
            skPoint(sketch, "E21.centerSnap0", {"position": v(761.01, -96.84) * mm});
            skPoint(sketch, "E21.centerSnap1", {"position": v(741.96, -71.44) * mm});
            skSolve(sketch);
        }
        {
            var Q0;
            Q0=qSketchRegion(id+"F21",true);
            extrude(context, id + "F22", {"entities" : qUnion([Q0]), "operationType" : NewBodyOperationType.REMOVE, "oppositeDirection" : true, "depth" : 6.35 * mm});
        }
        {
            var Q0;
            Q0=makeQuery(id+"F20.opExtrude","SWEPT_FACE",FACE,{"disambiguationData":[OSD([sQuery(id+"F19.wireOp",EDGE,"E20.top")])]});
            var sketch = newSketch(context, id + "F23", { "sketchPlane" : qUnion([Q0])});
            skLineSegment(sketch, "E22.bottom", {"start": v(-764.19, -53.98) * mm, "end": v(-757.84, -53.98) * mm});
            skLineSegment(sketch, "E22.top", {"start": v(-764.19, -88.9) * mm, "end": v(-757.84, -88.9) * mm});
            skLineSegment(sketch, "E22.left", {"start": v(-764.19, -53.98) * mm, "end": v(-764.19, -88.9) * mm});
            skLineSegment(sketch, "E22.right", {"start": v(-757.84, -53.98) * mm, "end": v(-757.84, -88.9) * mm});
            skPoint(sketch, "E22.middle", {"position": v(-761.01, -71.44) * mm});
            skPoint(sketch, "E22.middle.positionSnap0", {"position": v(-741.96, -71.44) * mm});
            skPoint(sketch, "E22.middle.positionSnap1", {"position": v(-761.01, -46.04) * mm});
            skPoint(sketch, "E22.centerSnap0", {"position": v(-741.96, -71.44) * mm});
            skPoint(sketch, "E22.centerSnap1", {"position": v(-761.01, -46.04) * mm});
            skSolve(sketch);
        }
        {
            var Q0;
            Q0=qSketchRegion(id+"F23",true);
            extrude(context, id + "F24", {"entities" : qUnion([Q0]), "operationType" : NewBodyOperationType.REMOVE, "oppositeDirection" : true, "depth" : 6.35 * mm});
        }
        {
            var Q0;
            Q0=makeQuery(id+"F22.boolean.opBoolean","COPY",EDGE,{"derivedFrom":makeQuery(id+"F22.opExtrude","SWEPT_EDGE",EDGE,{"disambiguationData":[OSD([sQuery(id+"F21.wireOp",EDGE,"E21.top"),sQuery(id+"F21.wireOp",EDGE,"E21.left")])]})});
            var Q1;
            Q1=makeQuery(id+"F22.boolean.opBoolean","COPY",EDGE,{"derivedFrom":makeQuery(id+"F22.opExtrude","SWEPT_EDGE",EDGE,{"disambiguationData":[OSD([sQuery(id+"F21.wireOp",EDGE,"E21.top"),sQuery(id+"F21.wireOp",EDGE,"E21.right")])]})});
            var Q2;
            Q2=makeQuery(id+"F22.boolean.opBoolean","COPY",EDGE,{"derivedFrom":makeQuery(id+"F22.opExtrude","SWEPT_EDGE",EDGE,{"disambiguationData":[OSD([sQuery(id+"F21.wireOp",EDGE,"E21.bottom"),sQuery(id+"F21.wireOp",EDGE,"E21.right")])]})});
            var Q3;
            Q3=makeQuery(id+"F22.boolean.opBoolean","COPY",EDGE,{"derivedFrom":makeQuery(id+"F22.opExtrude","SWEPT_EDGE",EDGE,{"disambiguationData":[OSD([sQuery(id+"F21.wireOp",EDGE,"E21.bottom"),sQuery(id+"F21.wireOp",EDGE,"E21.left")])]})});
            var Q4;
            Q4=makeQuery(id+"F24.boolean.opBoolean","COPY",EDGE,{"derivedFrom":makeQuery(id+"F24.opExtrude","SWEPT_EDGE",EDGE,{"disambiguationData":[OSD([sQuery(id+"F23.wireOp",EDGE,"E22.bottom"),sQuery(id+"F23.wireOp",EDGE,"E22.left")])]})});
            var Q5;
            Q5=makeQuery(id+"F24.boolean.opBoolean","COPY",EDGE,{"derivedFrom":makeQuery(id+"F24.opExtrude","SWEPT_EDGE",EDGE,{"disambiguationData":[OSD([sQuery(id+"F23.wireOp",EDGE,"E22.bottom"),sQuery(id+"F23.wireOp",EDGE,"E22.right")])]})});
            var Q6;
            Q6=makeQuery(id+"F24.boolean.opBoolean","COPY",EDGE,{"derivedFrom":makeQuery(id+"F24.opExtrude","SWEPT_EDGE",EDGE,{"disambiguationData":[OSD([sQuery(id+"F23.wireOp",EDGE,"E22.top"),sQuery(id+"F23.wireOp",EDGE,"E22.right")])]})});
            var Q7;
            Q7=makeQuery(id+"F24.boolean.opBoolean","COPY",EDGE,{"derivedFrom":makeQuery(id+"F24.opExtrude","SWEPT_EDGE",EDGE,{"disambiguationData":[OSD([sQuery(id+"F23.wireOp",EDGE,"E22.top"),sQuery(id+"F23.wireOp",EDGE,"E22.left")])]})});
            fillet(context, id + "F25", {"entities" : qUnion([Q0, Q1, Q2, Q3, Q4, Q5, Q6, Q7]), "radius" : 3.17 * mm, "tangentPropagation" : true, "allowEdgeOverflow" : false});
        }
        {
            var Q0;
            Q0=makeQuery(id+"F20.opExtrude","CAP_EDGE",EDGE,{"disambiguationData":[OSD([sQuery(id+"F19.wireOp",EDGE,"E19.right")])],"isStart":false});
            var Q1;
            Q1=makeQuery(id+"F20.opExtrude","CAP_EDGE",EDGE,{"disambiguationData":[OSD([sQuery(id+"F19.wireOp",EDGE,"E19.left")])],"isStart":false});
            var Q2;
            Q2=makeQuery(id+"F20.opExtrude","CAP_EDGE",EDGE,{"disambiguationData":[OSD([sQuery(id+"F19.wireOp",EDGE,"E20.left")])],"isStart":false});
            var Q3;
            Q3=makeQuery(id+"F20.opExtrude","CAP_EDGE",EDGE,{"disambiguationData":[OSD([sQuery(id+"F19.wireOp",EDGE,"E20.right")])],"isStart":false});
            fillet(context, id + "F26", {"entities" : qUnion([Q0, Q1, Q2, Q3]), "radius" : 19.05 * mm, "tangentPropagation" : true, "allowEdgeOverflow" : false});
        }
        {
            var Q0;
            Q0=makeQuery(id+"F7.boolean.opBoolean","COPY",FACE,{"derivedFrom":makeQuery(id+"F7.opExtrude","SWEPT_FACE",FACE,{"disambiguationData":[OSD([sQuery(id+"F6.wireOp",EDGE,"E12")])]})});
            var sketch = newSketch(context, id + "F27", { "sketchPlane" : qUnion([Q0])});
            skLineSegment(sketch, "E23.bottom", {"start": v(139.76, 95.83) * mm, "end": v(171.51, 95.83) * mm});
            skLineSegment(sketch, "E23.top", {"start": v(139.76, 133.93) * mm, "end": v(171.51, 133.93) * mm});
            skLineSegment(sketch, "E23.left", {"start": v(139.76, 95.83) * mm, "end": v(139.76, 133.93) * mm});
            skLineSegment(sketch, "E23.right", {"start": v(171.51, 95.83) * mm, "end": v(171.51, 133.93) * mm});
            skPoint(sketch, "E23.middle", {"position": v(155.64, 114.88) * mm});
            skPoint(sketch, "E23.middle.positionSnap0", {"position": v(155.64, 198) * mm});
            skPoint(sketch, "E23.middle.positionSnap1", {"position": v(268.73, 114.88) * mm});
            skPoint(sketch, "E23.centerSnap0", {"position": v(155.64, 198) * mm});
            skPoint(sketch, "E23.centerSnap1", {"position": v(268.73, 114.88) * mm});
            skSolve(sketch);
        }
        {
            var Q0;
            Q0=qSketchRegion(id+"F27",true);
            extrude(context, id + "F28", {"entities" : qUnion([Q0]), "operationType" : NewBodyOperationType.REMOVE, "oppositeDirection" : true, "depth" : 4.78 * mm});
        }
        {
            var Q0;
            Q0=makeQuery(id+"F7.boolean.opBoolean","COPY",FACE,{"derivedFrom":makeQuery(id+"F7.opExtrude","SWEPT_FACE",FACE,{"disambiguationData":[OSD([sQuery(id+"F6.wireOp",EDGE,"E10")])]})});
            var sketch = newSketch(context, id + "F29", { "sketchPlane" : qUnion([Q0])});
            skLineSegment(sketch, "E24.bottom", {"start": v(-171.51, 133.93) * mm, "end": v(-139.76, 133.93) * mm});
            skLineSegment(sketch, "E24.top", {"start": v(-171.51, 95.83) * mm, "end": v(-139.76, 95.83) * mm});
            skLineSegment(sketch, "E24.left", {"start": v(-171.51, 133.93) * mm, "end": v(-171.51, 95.83) * mm});
            skLineSegment(sketch, "E24.right", {"start": v(-139.76, 133.93) * mm, "end": v(-139.76, 95.83) * mm});
            skPoint(sketch, "E24.middle", {"position": v(-155.64, 114.88) * mm});
            skPoint(sketch, "E24.middle.positionSnap0", {"position": v(-155.64, 198) * mm});
            skPoint(sketch, "E24.middle.positionSnap1", {"position": v(-268.73, 114.88) * mm});
            skPoint(sketch, "E24.centerSnap0", {"position": v(-155.64, 198) * mm});
            skPoint(sketch, "E24.centerSnap1", {"position": v(-268.73, 114.88) * mm});
            skSolve(sketch);
        }
        {
            var Q0;
            Q0=qSketchRegion(id+"F29",true);
            extrude(context, id + "F30", {"entities" : qUnion([Q0]), "operationType" : NewBodyOperationType.REMOVE, "oppositeDirection" : true, "depth" : 4.78 * mm});
        }
        {
            var Q0;
            Q0=makeQuery(id+"F5.boolean.opBoolean","COPY",FACE,{"derivedFrom":makeQuery(id+"F5.opExtrude","SWEPT_FACE",FACE,{"disambiguationData":[OSD([sQuery(id+"F4.wireOp",EDGE,"E7")])]})});
            var sketch = newSketch(context, id + "F31", { "sketchPlane" : qUnion([Q0])});
            skLineSegment(sketch, "E25", {"start": v(-862.82, 88.9) * mm, "end": v(-166.61, 88.9) * mm});
            skLineSegment(sketch, "E26", {"start": v(-166.61, 88.9) * mm, "end": v(-310.48, -82.55) * mm});
            skLineSegment(sketch, "E27", {"start": v(-310.48, -82.55) * mm, "end": v(-862.82, -82.55) * mm});
            skLineSegment(sketch, "E28", {"start": v(-862.82, -82.55) * mm, "end": v(-862.82, 88.9) * mm});
            skLineSegment(sketch, "E29.MirrorCS", {"start": v(862.82, 88.9) * mm, "end": v(166.61, 88.9) * mm});
            skLineSegment(sketch, "E30.MirrorCS", {"start": v(862.82, -82.55) * mm, "end": v(862.82, 88.9) * mm});
            skLineSegment(sketch, "E31.MirrorCS", {"start": v(310.48, -82.55) * mm, "end": v(862.82, -82.55) * mm});
            skLineSegment(sketch, "E32.MirrorCS", {"start": v(166.61, 88.9) * mm, "end": v(310.48, -82.55) * mm});
            skSolve(sketch);
        }
        {
            var Q0;
            Q0=qSketchRegion(id+"F31",true);
            extrude(context, id + "F32", {"entities" : qUnion([Q0]), "depth" : 3.17 * mm});
        }
        {
            var Q0;
            Q0=makeQuery(id+"F7.boolean.opBoolean","COPY",FACE,{"derivedFrom":makeQuery(id+"F7.opExtrude","CAP_FACE",FACE,{"disambiguationData":[OSD([sQuery(id+"F4.wireOp",EDGE,"E7"),sQuery(id+"F6.wireOp",EDGE,"E10"),sQuery(id+"F6.wireOp",EDGE,"E11"),sQuery(id+"F6.wireOp",EDGE,"E12")])],"isStart":false})});
            var sketch = newSketch(context, id + "F33", { "sketchPlane" : qUnion([Q0])});
            skLineSegment(sketch, "E33", {"start": v(-143.52, 57.15) * mm, "end": v(143.52, 57.15) * mm});
            skLineSegment(sketch, "E34", {"start": v(143.52, 57.15) * mm, "end": v(260.74, -82.55) * mm});
            skLineSegment(sketch, "E35", {"start": v(260.74, -82.55) * mm, "end": v(-260.74, -82.55) * mm});
            skLineSegment(sketch, "E36", {"start": v(-260.74, -82.55) * mm, "end": v(-143.52, 57.15) * mm});
            skSolve(sketch);
        }
        {
            var Q0;
            Q0=qSketchRegion(id+"F33",true);
            extrude(context, id + "F34", {"entities" : qUnion([Q0]), "depth" : 3.17 * mm});
        }
        {
            var Q0;
            Q0=makeQuery(id+"F32.opExtrude","SWEPT_EDGE",EDGE,{"disambiguationData":[OSD([sQuery(id+"F31.wireOp",EDGE,"E26"),sQuery(id+"F31.wireOp",EDGE,"E27")])]});
            var Q1;
            Q1=makeQuery(id+"F32.opExtrude","SWEPT_EDGE",EDGE,{"disambiguationData":[OSD([sQuery(id+"F31.wireOp",EDGE,"E31.MirrorCS"),sQuery(id+"F31.wireOp",EDGE,"E32.MirrorCS")])]});
            var Q2;
            Q2=makeQuery(id+"F32.opExtrude","SWEPT_EDGE",EDGE,{"disambiguationData":[OSD([sQuery(id+"F31.wireOp",EDGE,"E30.MirrorCS"),sQuery(id+"F31.wireOp",EDGE,"E31.MirrorCS")])]});
            var Q3;
            Q3=makeQuery(id+"F34.opExtrude","SWEPT_EDGE",EDGE,{"disambiguationData":[OSD([sQuery(id+"F33.wireOp",EDGE,"E35"),sQuery(id+"F33.wireOp",EDGE,"E36")])]});
            var Q4;
            Q4=makeQuery(id+"F34.opExtrude","SWEPT_EDGE",EDGE,{"disambiguationData":[OSD([sQuery(id+"F33.wireOp",EDGE,"E34"),sQuery(id+"F33.wireOp",EDGE,"E35")])]});
            var Q5;
            Q5=makeQuery(id+"F34.opExtrude","SWEPT_EDGE",EDGE,{"disambiguationData":[OSD([sQuery(id+"F33.wireOp",EDGE,"E33"),sQuery(id+"F33.wireOp",EDGE,"E34")])]});
            var Q6;
            Q6=makeQuery(id+"F34.opExtrude","SWEPT_EDGE",EDGE,{"disambiguationData":[OSD([sQuery(id+"F33.wireOp",EDGE,"E33"),sQuery(id+"F33.wireOp",EDGE,"E36")])]});
            var Q7;
            Q7=makeQuery(id+"F32.opExtrude","SWEPT_EDGE",EDGE,{"disambiguationData":[OSD([sQuery(id+"F31.wireOp",EDGE,"E29.MirrorCS"),sQuery(id+"F31.wireOp",EDGE,"E30.MirrorCS")])]});
            var Q8;
            Q8=makeQuery(id+"F32.opExtrude","SWEPT_EDGE",EDGE,{"disambiguationData":[OSD([sQuery(id+"F31.wireOp",EDGE,"E29.MirrorCS"),sQuery(id+"F31.wireOp",EDGE,"E32.MirrorCS")])]});
            var Q9;
            Q9=makeQuery(id+"F32.opExtrude","SWEPT_EDGE",EDGE,{"disambiguationData":[OSD([sQuery(id+"F31.wireOp",EDGE,"E25"),sQuery(id+"F31.wireOp",EDGE,"E26")])]});
            var Q10;
            Q10=makeQuery(id+"F32.opExtrude","SWEPT_EDGE",EDGE,{"disambiguationData":[OSD([sQuery(id+"F31.wireOp",EDGE,"E25"),sQuery(id+"F31.wireOp",EDGE,"E28")])]});
            fillet(context, id + "F35", {"entities" : qUnion([Q0, Q1, Q2, Q3, Q4, Q5, Q6, Q7, Q8, Q9, Q10]), "radius" : 3.17 * mm, "tangentPropagation" : true, "allowEdgeOverflow" : false});
        }
        {
            var Q0;
            Q0=makeQuery(id+"F7.boolean.opBoolean","COPY",FACE,{"derivedFrom":makeQuery(id+"F7.opExtrude","SWEPT_FACE",FACE,{"disambiguationData":[OSD([sQuery(id+"F6.wireOp",EDGE,"E11")])]})});
            var sketch = newSketch(context, id + "F36", { "sketchPlane" : qUnion([Q0])});
            skLineSegment(sketch, "E37.bottom", {"start": v(139.7, 51.38) * mm, "end": v(-139.7, 51.38) * mm});
            skLineSegment(sketch, "E37.top", {"start": v(139.7, 178.38) * mm, "end": v(-139.7, 178.38) * mm});
            skLineSegment(sketch, "E37.left", {"start": v(139.7, 51.38) * mm, "end": v(139.7, 178.38) * mm});
            skLineSegment(sketch, "E37.right", {"start": v(-139.7, 51.38) * mm, "end": v(-139.7, 178.38) * mm});
            skPoint(sketch, "E37.middle", {"position": v(0, 114.88) * mm});
            skPoint(sketch, "E37.middle.positionSnap0", {"position": v(-149.44, 114.88) * mm});
            skPoint(sketch, "E37.middle.positionSnap1", {"position": v(0, 198) * mm});
            skPoint(sketch, "E37.centerSnap0", {"position": v(-149.44, 114.88) * mm});
            skPoint(sketch, "E37.centerSnap1", {"position": v(0, 198) * mm});
            skSolve(sketch);
        }
        {
            var Q0;
            Q0=qSketchRegion(id+"F36",true);
            extrude(context, id + "F37", {"entities" : qUnion([Q0]), "depth" : 3.17 * mm});
        }
        {
            var Q0;
            Q0=makeQuery(id+"F37.opExtrude","CAP_FACE",FACE,{"disambiguationData":[OSD([sQuery(id+"F36.wireOp",EDGE,"E37.bottom"),sQuery(id+"F36.wireOp",EDGE,"E37.top"),sQuery(id+"F36.wireOp",EDGE,"E37.left"),sQuery(id+"F36.wireOp",EDGE,"E37.right")])],"isStart":false});
            var sketch = newSketch(context, id + "F38", { "sketchPlane" : qUnion([Q0])});
            skText(sketch, "E38", { "text": "ABC - 123", "fontName": "AllertaStencil-Regular.ttf"});
            const initialGuessF38  = {"E38": [-0.127, 0.09792, 1, 0, 0.0394]};
            skSetInitialGuess(sketch, initialGuessF38);
            skSolve(sketch);
        }
        {
            var Q0;
            Q0=qSketchRegion(id+"F38",true);
            extrude(context, id + "F39", {"entities" : qUnion([Q0]), "operationType" : NewBodyOperationType.REMOVE, "oppositeDirection" : true, "depth" : 3.17 * mm});
        }
        {
            var Q0;
            Q0=makeQuery(id+"F37.opExtrude","CAP_FACE",FACE,{"disambiguationData":[OSD([sQuery(id+"F36.wireOp",EDGE,"E37.bottom"),sQuery(id+"F36.wireOp",EDGE,"E37.top"),sQuery(id+"F36.wireOp",EDGE,"E37.left"),sQuery(id+"F36.wireOp",EDGE,"E37.right")])],"isStart":false});
            var sketch = newSketch(context, id + "F40", { "sketchPlane" : qUnion([Q0])});
            skCircle(sketch, "E39", {"center": v(-127, 168.85) * mm, "radius": 3.18 * mm});
            skCircle(sketch, "E40", {"center": v(127, 168.84) * mm, "radius": 3.18 * mm});
            skCircle(sketch, "E41", {"center": v(125.6, 57.73) * mm, "radius": 3.18 * mm});
            skCircle(sketch, "E42", {"center": v(-128.4, 57.73) * mm, "radius": 3.18 * mm});
            skSolve(sketch);
        }
        {
            var Q0;
            Q0=qSketchRegion(id+"F40",true);
            extrude(context, id + "F41", {"entities" : qUnion([Q0]), "operationType" : NewBodyOperationType.REMOVE, "endBound" : BoundingType.THROUGH_ALL, "oppositeDirection" : true, "depth" : 25.4 * mm});
        }
        {
            var Q0;
            Q0=makeQuery(id+"F37.opExtrude","SWEPT_EDGE",EDGE,{"disambiguationData":[OSD([sQuery(id+"F36.wireOp",EDGE,"E37.top"),sQuery(id+"F36.wireOp",EDGE,"E37.right")])]});
            var Q1;
            Q1=makeQuery(id+"F37.opExtrude","SWEPT_EDGE",EDGE,{"disambiguationData":[OSD([sQuery(id+"F36.wireOp",EDGE,"E37.top"),sQuery(id+"F36.wireOp",EDGE,"E37.left")])]});
            var Q2;
            Q2=makeQuery(id+"F37.opExtrude","SWEPT_EDGE",EDGE,{"disambiguationData":[OSD([sQuery(id+"F36.wireOp",EDGE,"E37.bottom"),sQuery(id+"F36.wireOp",EDGE,"E37.left")])]});
            var Q3;
            Q3=makeQuery(id+"F37.opExtrude","SWEPT_EDGE",EDGE,{"disambiguationData":[OSD([sQuery(id+"F36.wireOp",EDGE,"E37.bottom"),sQuery(id+"F36.wireOp",EDGE,"E37.right")])]});
            fillet(context, id + "F42", {"entities" : qUnion([Q0, Q1, Q2, Q3]), "radius" : 3.17 * mm, "tangentPropagation" : true, "allowEdgeOverflow" : false});
        }
        {
            var Q0;
            Q0=makeQuery(id+"F17.boolean.opBoolean","COPY",EDGE,{"derivedFrom":makeQuery(id+"F17.opExtrude","SWEPT_EDGE",EDGE,{"disambiguationData":[OSD([sQuery(id+"F16.wireOp",EDGE,"E18.top"),sQuery(id+"F16.wireOp",EDGE,"E18.left")])]})});
            var Q1;
            Q1=makeQuery(id+"F17.boolean.opBoolean","COPY",EDGE,{"derivedFrom":makeQuery(id+"F17.opExtrude","SWEPT_EDGE",EDGE,{"disambiguationData":[OSD([sQuery(id+"F16.wireOp",EDGE,"E18.bottom"),sQuery(id+"F16.wireOp",EDGE,"E18.left")])]})});
            var Q2;
            Q2=makeQuery(id+"F17.boolean.opBoolean","COPY",EDGE,{"derivedFrom":makeQuery(id+"F17.opExtrude","SWEPT_EDGE",EDGE,{"disambiguationData":[OSD([sQuery(id+"F16.wireOp",EDGE,"E18.top"),sQuery(id+"F16.wireOp",EDGE,"E18.right")])]})});
            var Q3;
            Q3=makeQuery(id+"F17.boolean.opBoolean","COPY",EDGE,{"derivedFrom":makeQuery(id+"F17.opExtrude","SWEPT_EDGE",EDGE,{"disambiguationData":[OSD([sQuery(id+"F16.wireOp",EDGE,"E18.bottom"),sQuery(id+"F16.wireOp",EDGE,"E18.right")])]})});
            fillet(context, id + "F43", {"entities" : qUnion([Q0, Q1, Q2, Q3]), "radius" : 6.35 * mm, "tangentPropagation" : true, "allowEdgeOverflow" : false});
        }
        {
            var Q0;
            Q0=makeQuery(id+"F15.opShell","OFFSET_FACE",FACE,{"disambiguationData":[OSD([sQuery(id+"F0.wireOp",EDGE,"E0.bottom")])]});
            var sketch = newSketch(context, id + "F44", { "sketchPlane" : qUnion([Q0])});
            skLineSegment(sketch, "E43.bottom", {"start": v(-560.99, 160.92) * mm, "end": v(-554.64, 160.92) * mm});
            skLineSegment(sketch, "E43.top", {"start": v(-560.99, 59.32) * mm, "end": v(-554.64, 59.32) * mm});
            skLineSegment(sketch, "E43.left", {"start": v(-560.99, 160.92) * mm, "end": v(-560.99, 59.32) * mm});
            skLineSegment(sketch, "E43.right", {"start": v(-554.64, 160.92) * mm, "end": v(-554.64, 59.32) * mm});
            skPoint(sketch, "E43.middle", {"position": v(-557.81, 110.12) * mm});
            skPoint(sketch, "E43.middle.positionSnap0", {"position": v(-303.81, 110.12) * mm});
            skPoint(sketch, "E43.centerSnap0", {"position": v(-303.81, 110.12) * mm});
            skLineSegment(sketch, "E44.bottom", {"start": v(554.64, 160.92) * mm, "end": v(560.99, 160.92) * mm});
            skLineSegment(sketch, "E44.top", {"start": v(554.64, 59.32) * mm, "end": v(560.99, 59.32) * mm});
            skLineSegment(sketch, "E44.left", {"start": v(554.64, 160.92) * mm, "end": v(554.64, 59.32) * mm});
            skLineSegment(sketch, "E44.right", {"start": v(560.99, 160.92) * mm, "end": v(560.99, 59.32) * mm});
            skPoint(sketch, "E44.middle", {"position": v(557.81, 110.12) * mm});
            skPoint(sketch, "E44.middle.positionSnap0", {"position": v(303.81, 110.12) * mm});
            skPoint(sketch, "E44.centerSnap0", {"position": v(303.81, 110.12) * mm});
            skSolve(sketch);
        }
        {
            var Q0;
            Q0=qSketchRegion(id+"F44",true);
            extrude(context, id + "F45", {"entities" : qUnion([Q0]), "depth" : 304.8 * mm});
        }
        {
            var Q0;
            Q0=makeQuery(id+"F45.opExtrude","SWEPT_FACE",FACE,{"disambiguationData":[OSD([sQuery(id+"F44.wireOp",EDGE,"E43.left")])]});
            var sketch = newSketch(context, id + "F46", { "sketchPlane" : qUnion([Q0])});
            skLineSegment(sketch, "E45", {"start": v(101.89, 59.32) * mm, "end": v(149.87, 110.12) * mm});
            skPoint(sketch, "E45.endSnap0", {"position": v(207.96, 110.12) * mm});
            skLineSegment(sketch, "E46", {"start": v(149.87, 110.12) * mm, "end": v(207.96, 110.12) * mm});
            skSolve(sketch);
        }
        {
            var Q0;
            {var subQ0=sQuery(id+"F46.wireOp",EDGE,"E45");Q0=makeQuery(id+"F46.imprint","IMPRINT",FACE,{"disambiguationData":[TD([[makeQuery(id+"F46.imprint","IMPRINT",EDGE,{"derivedFrom":subQ0}),-1.0]])]});}
            extrude(context, id + "F47", {"entities" : qUnion([Q0]), "operationType" : NewBodyOperationType.REMOVE, "endBound" : BoundingType.THROUGH_ALL, "oppositeDirection" : true, "depth" : 25.4 * mm});
        }
        {
            var Q0;
            Q0=makeQuery(id+"F45.opExtrude","CAP_EDGE",EDGE,{"disambiguationData":[OSD([sQuery(id+"F44.wireOp",EDGE,"E43.bottom")])],"isStart":false});
            var Q1;
            {var subQ0=sQuery(id+"F44.wireOp",EDGE,"E43.left");var subQ1=sQuery(id+"F46.wireOp",EDGE,"E46");Q1=makeQuery(id+"F47.boolean.opBoolean","COPY",EDGE,{"disambiguationData":[topologyDisambiguationEdgeConnected([makeQuery(id+"F45.opExtrude","CAP_FACE",FACE,{"disambiguationData":[OSD([sQuery(id+"F44.wireOp",EDGE,"E43.bottom"),sQuery(id+"F44.wireOp",EDGE,"E43.top"),subQ0,sQuery(id+"F44.wireOp",EDGE,"E43.right")])],"isStart":false})])],"derivedFrom":makeQuery(id+"F47.opExtrude","SWEPT_EDGE",EDGE,{"disambiguationData":[OSD([subQ0,subQ1])]})});}
            var Q2;
            {var subQ0=sQuery(id+"F46.wireOp",EDGE,"E45");var subQ1=sQuery(id+"F46.wireOp",EDGE,"E46");Q2=makeQuery(id+"F47.boolean.opBoolean","COPY",EDGE,{"disambiguationData":[TD([makeQuery(id+"F45.opExtrude","SWEPT_FACE",FACE,{"disambiguationData":[OSD([sQuery(id+"F44.wireOp",EDGE,"E43.left")])]})])],"derivedFrom":makeQuery(id+"F47.opExtrude","SWEPT_EDGE",EDGE,{"disambiguationData":[OSD([subQ0,subQ1])]})});}
            var Q3;
            {var subQ0=sQuery(id+"F44.wireOp",EDGE,"E43.top");var subQ1=sQuery(id+"F46.wireOp",EDGE,"E45");Q3=makeQuery(id+"F47.boolean.opBoolean","COPY",EDGE,{"disambiguationData":[topologyDisambiguationEdgeConnected([makeQuery(id+"F45.opExtrude","SWEPT_FACE",FACE,{"disambiguationData":[OSD([subQ0])]})])],"derivedFrom":makeQuery(id+"F47.opExtrude","SWEPT_EDGE",EDGE,{"disambiguationData":[OSD([subQ0,sQuery(id+"F44.wireOp",EDGE,"E43.left"),subQ1])]})});}
            var Q4;
            {var subQ0=sQuery(id+"F46.wireOp",EDGE,"E45");Q4=makeQuery(id+"F47.boolean.opBoolean","COPY",EDGE,{"disambiguationData":[topologyDisambiguationEdgeConnected([makeQuery(id+"F45.opExtrude","SWEPT_FACE",FACE,{"disambiguationData":[OSD([sQuery(id+"F44.wireOp",EDGE,"E44.top")])]})])],"derivedFrom":makeQuery(id+"F47.opExtrude","SWEPT_EDGE",EDGE,{"disambiguationData":[OSD([sQuery(id+"F44.wireOp",EDGE,"E43.top"),sQuery(id+"F44.wireOp",EDGE,"E43.left"),subQ0])]})});}
            var Q5;
            {var subQ0=sQuery(id+"F46.wireOp",EDGE,"E46");var subQ1=sQuery(id+"F46.wireOp",EDGE,"E45");Q5=makeQuery(id+"F47.boolean.opBoolean","COPY",EDGE,{"disambiguationData":[TD([makeQuery(id+"F45.opExtrude","SWEPT_FACE",FACE,{"disambiguationData":[OSD([sQuery(id+"F44.wireOp",EDGE,"E44.left")])]})])],"derivedFrom":makeQuery(id+"F47.opExtrude","SWEPT_EDGE",EDGE,{"disambiguationData":[OSD([subQ1,subQ0])]})});}
            var Q6;
            {var subQ0=sQuery(id+"F46.wireOp",EDGE,"E46");Q6=makeQuery(id+"F47.boolean.opBoolean","COPY",EDGE,{"disambiguationData":[topologyDisambiguationEdgeConnected([makeQuery(id+"F45.opExtrude","CAP_FACE",FACE,{"disambiguationData":[OSD([sQuery(id+"F44.wireOp",EDGE,"E44.bottom"),sQuery(id+"F44.wireOp",EDGE,"E44.top"),sQuery(id+"F44.wireOp",EDGE,"E44.left"),sQuery(id+"F44.wireOp",EDGE,"E44.right")])],"isStart":false})])],"derivedFrom":makeQuery(id+"F47.opExtrude","SWEPT_EDGE",EDGE,{"disambiguationData":[OSD([sQuery(id+"F44.wireOp",EDGE,"E43.left"),subQ0])]})});}
            var Q7;
            Q7=makeQuery(id+"F45.opExtrude","CAP_EDGE",EDGE,{"disambiguationData":[OSD([sQuery(id+"F44.wireOp",EDGE,"E44.bottom")])],"isStart":false});
            fillet(context, id + "F48", {"entities" : qUnion([Q0, Q1, Q2, Q3, Q4, Q5, Q6, Q7]), "radius" : 3.17 * mm, "tangentPropagation" : true, "allowEdgeOverflow" : false});
        }
        {
            var Q0;
            Q0=makeQuery(id+"F45.opExtrude","SWEPT_FACE",FACE,{"disambiguationData":[OSD([sQuery(id+"F44.wireOp",EDGE,"E43.left")])]});
            var sketch = newSketch(context, id + "F49", { "sketchPlane" : qUnion([Q0])});
            skCircle(sketch, "E47", {"center": v(178.01, 135.52) * mm, "radius": 11.11 * mm});
            skPoint(sketch, "E47.centerSnap0", {"position": v(207.96, 135.52) * mm});
            skPoint(sketch, "E47.centerSnap1", {"position": v(178.01, 110.12) * mm});
            skLineSegment(sketch, "E48.bottom", {"start": v(120.76, 136.37) * mm, "end": v(108.06, 136.37) * mm});
            skLineSegment(sketch, "E48.top", {"start": v(120.76, 98.27) * mm, "end": v(108.06, 98.27) * mm});
            skLineSegment(sketch, "E48.left", {"start": v(120.76, 136.37) * mm, "end": v(120.76, 98.27) * mm});
            skLineSegment(sketch, "E48.right", {"start": v(108.06, 136.37) * mm, "end": v(108.06, 98.27) * mm});
            skSolve(sketch);
        }
        {
            var Q0;
            Q0=qSketchRegion(id+"F49",true);
            extrude(context, id + "F50", {"entities" : qUnion([Q0]), "operationType" : NewBodyOperationType.REMOVE, "endBound" : BoundingType.THROUGH_ALL, "oppositeDirection" : true, "depth" : 25.4 * mm});
        }
        {
            var Q0;
            {var subQ0=sQuery(id+"F49.wireOp",EDGE,"E48.bottom");var subQ1=sQuery(id+"F49.wireOp",EDGE,"E48.right");Q0=makeQuery(id+"F50.boolean.opBoolean","COPY",EDGE,{"disambiguationData":[TD([makeQuery(id+"F45.opExtrude","SWEPT_FACE",FACE,{"disambiguationData":[OSD([sQuery(id+"F44.wireOp",EDGE,"E43.left")])]})])],"derivedFrom":makeQuery(id+"F50.opExtrude","SWEPT_EDGE",EDGE,{"disambiguationData":[OSD([subQ0,subQ1])]})});}
            var Q1;
            {var subQ0=sQuery(id+"F49.wireOp",EDGE,"E48.top");var subQ1=sQuery(id+"F49.wireOp",EDGE,"E48.right");Q1=makeQuery(id+"F50.boolean.opBoolean","COPY",EDGE,{"disambiguationData":[TD([makeQuery(id+"F45.opExtrude","SWEPT_FACE",FACE,{"disambiguationData":[OSD([sQuery(id+"F44.wireOp",EDGE,"E43.left")])]})])],"derivedFrom":makeQuery(id+"F50.opExtrude","SWEPT_EDGE",EDGE,{"disambiguationData":[OSD([subQ0,subQ1])]})});}
            var Q2;
            {var subQ0=sQuery(id+"F49.wireOp",EDGE,"E48.top");var subQ1=sQuery(id+"F49.wireOp",EDGE,"E48.left");Q2=makeQuery(id+"F50.boolean.opBoolean","COPY",EDGE,{"disambiguationData":[TD([makeQuery(id+"F45.opExtrude","SWEPT_FACE",FACE,{"disambiguationData":[OSD([sQuery(id+"F44.wireOp",EDGE,"E43.left")])]})])],"derivedFrom":makeQuery(id+"F50.opExtrude","SWEPT_EDGE",EDGE,{"disambiguationData":[OSD([subQ0,subQ1])]})});}
            var Q3;
            {var subQ0=sQuery(id+"F49.wireOp",EDGE,"E48.left");var subQ1=sQuery(id+"F49.wireOp",EDGE,"E48.bottom");Q3=makeQuery(id+"F50.boolean.opBoolean","COPY",EDGE,{"disambiguationData":[TD([makeQuery(id+"F45.opExtrude","SWEPT_FACE",FACE,{"disambiguationData":[OSD([sQuery(id+"F44.wireOp",EDGE,"E43.left")])]})])],"derivedFrom":makeQuery(id+"F50.opExtrude","SWEPT_EDGE",EDGE,{"disambiguationData":[OSD([subQ1,subQ0])]})});}
            var Q4;
            {var subQ0=sQuery(id+"F49.wireOp",EDGE,"E48.right");var subQ1=sQuery(id+"F49.wireOp",EDGE,"E48.top");Q4=makeQuery(id+"F50.boolean.opBoolean","COPY",EDGE,{"disambiguationData":[TD([makeQuery(id+"F45.opExtrude","SWEPT_FACE",FACE,{"disambiguationData":[OSD([sQuery(id+"F44.wireOp",EDGE,"E44.left")])]})])],"derivedFrom":makeQuery(id+"F50.opExtrude","SWEPT_EDGE",EDGE,{"disambiguationData":[OSD([subQ1,subQ0])]})});}
            var Q5;
            {var subQ0=sQuery(id+"F49.wireOp",EDGE,"E48.left");var subQ1=sQuery(id+"F49.wireOp",EDGE,"E48.top");Q5=makeQuery(id+"F50.boolean.opBoolean","COPY",EDGE,{"disambiguationData":[TD([makeQuery(id+"F45.opExtrude","SWEPT_FACE",FACE,{"disambiguationData":[OSD([sQuery(id+"F44.wireOp",EDGE,"E44.left")])]})])],"derivedFrom":makeQuery(id+"F50.opExtrude","SWEPT_EDGE",EDGE,{"disambiguationData":[OSD([subQ1,subQ0])]})});}
            var Q6;
            {var subQ0=sQuery(id+"F49.wireOp",EDGE,"E48.bottom");var subQ1=sQuery(id+"F49.wireOp",EDGE,"E48.right");Q6=makeQuery(id+"F50.boolean.opBoolean","COPY",EDGE,{"disambiguationData":[TD([makeQuery(id+"F45.opExtrude","SWEPT_FACE",FACE,{"disambiguationData":[OSD([sQuery(id+"F44.wireOp",EDGE,"E44.left")])]})])],"derivedFrom":makeQuery(id+"F50.opExtrude","SWEPT_EDGE",EDGE,{"disambiguationData":[OSD([subQ0,subQ1])]})});}
            var Q7;
            {var subQ0=sQuery(id+"F49.wireOp",EDGE,"E48.left");var subQ1=sQuery(id+"F49.wireOp",EDGE,"E48.bottom");Q7=makeQuery(id+"F50.boolean.opBoolean","COPY",EDGE,{"disambiguationData":[TD([makeQuery(id+"F45.opExtrude","SWEPT_FACE",FACE,{"disambiguationData":[OSD([sQuery(id+"F44.wireOp",EDGE,"E44.left")])]})])],"derivedFrom":makeQuery(id+"F50.opExtrude","SWEPT_EDGE",EDGE,{"disambiguationData":[OSD([subQ1,subQ0])]})});}
            fillet(context, id + "F51", {"entities" : qUnion([Q0, Q1, Q2, Q3, Q4, Q5, Q6, Q7]), "radius" : 6.35 * mm, "tangentPropagation" : true, "allowEdgeOverflow" : false});
        }
        {
            var Q0;
            Q0=makeQuery(id+"F45.opExtrude","SWEPT_FACE",FACE,{"disambiguationData":[OSD([sQuery(id+"F44.wireOp",EDGE,"E43.left")])]});
            var sketch = newSketch(context, id + "F52", { "sketchPlane" : qUnion([Q0])});
            skLineSegment(sketch, "E49.bottom", {"start": v(-44.45, 105.35) * mm, "end": v(44.45, 105.35) * mm});
            skLineSegment(sketch, "E49.top", {"start": v(-44.45, 114.88) * mm, "end": v(44.45, 114.88) * mm});
            skLineSegment(sketch, "E49.left", {"start": v(-44.45, 105.35) * mm, "end": v(-44.45, 114.88) * mm});
            skLineSegment(sketch, "E49.right", {"start": v(44.45, 105.35) * mm, "end": v(44.45, 114.88) * mm});
            skPoint(sketch, "E49.middle", {"position": v(0, 110.12) * mm});
            skPoint(sketch, "E49.middle.positionSnap0", {"position": v(-96.84, 110.12) * mm});
            skPoint(sketch, "E49.centerSnap0", {"position": v(-96.84, 110.12) * mm});
            skSolve(sketch);
        }
        {
            var Q0;
            Q0=qSketchRegion(id+"F52",true);
            extrude(context, id + "F53", {"entities" : qUnion([Q0]), "operationType" : NewBodyOperationType.REMOVE, "oppositeDirection" : true, "depth" : 6.35 * mm});
        }
        {
            var Q0;
            Q0=makeQuery(id+"F45.opExtrude","SWEPT_FACE",FACE,{"disambiguationData":[OSD([sQuery(id+"F44.wireOp",EDGE,"E44.right")])]});
            var sketch = newSketch(context, id + "F54", { "sketchPlane" : qUnion([Q0])});
            skLineSegment(sketch, "E50.bottom", {"start": v(-44.45, 105.35) * mm, "end": v(44.45, 105.35) * mm});
            skLineSegment(sketch, "E50.top", {"start": v(-44.45, 114.88) * mm, "end": v(44.45, 114.88) * mm});
            skLineSegment(sketch, "E50.left", {"start": v(-44.45, 105.35) * mm, "end": v(-44.45, 114.88) * mm});
            skLineSegment(sketch, "E50.right", {"start": v(44.45, 105.35) * mm, "end": v(44.45, 114.88) * mm});
            skPoint(sketch, "E50.middle", {"position": v(0, 110.12) * mm});
            skPoint(sketch, "E50.middle.positionSnap0", {"position": v(96.84, 110.12) * mm});
            skPoint(sketch, "E50.centerSnap0", {"position": v(96.84, 110.12) * mm});
            skSolve(sketch);
        }
        {
            var Q0;
            Q0=qSketchRegion(id+"F54",true);
            extrude(context, id + "F55", {"entities" : qUnion([Q0]), "operationType" : NewBodyOperationType.REMOVE, "oppositeDirection" : true, "depth" : 6.35 * mm});
        }
        {
            var Q0;
            Q0=makeQuery(id+"F55.boolean.opBoolean","COPY",EDGE,{"derivedFrom":makeQuery(id+"F55.opExtrude","SWEPT_EDGE",EDGE,{"disambiguationData":[OSD([sQuery(id+"F54.wireOp",EDGE,"E50.top"),sQuery(id+"F54.wireOp",EDGE,"E50.right")])]})});
            var Q1;
            Q1=makeQuery(id+"F55.boolean.opBoolean","COPY",EDGE,{"derivedFrom":makeQuery(id+"F55.opExtrude","SWEPT_EDGE",EDGE,{"disambiguationData":[OSD([sQuery(id+"F54.wireOp",EDGE,"E50.top"),sQuery(id+"F54.wireOp",EDGE,"E50.left")])]})});
            var Q2;
            Q2=makeQuery(id+"F55.boolean.opBoolean","COPY",EDGE,{"derivedFrom":makeQuery(id+"F55.opExtrude","SWEPT_EDGE",EDGE,{"disambiguationData":[OSD([sQuery(id+"F54.wireOp",EDGE,"E50.bottom"),sQuery(id+"F54.wireOp",EDGE,"E50.left")])]})});
            var Q3;
            Q3=makeQuery(id+"F53.boolean.opBoolean","COPY",EDGE,{"derivedFrom":makeQuery(id+"F53.opExtrude","SWEPT_EDGE",EDGE,{"disambiguationData":[OSD([sQuery(id+"F52.wireOp",EDGE,"E49.bottom"),sQuery(id+"F52.wireOp",EDGE,"E49.left")])]})});
            var Q4;
            Q4=makeQuery(id+"F53.boolean.opBoolean","COPY",EDGE,{"derivedFrom":makeQuery(id+"F53.opExtrude","SWEPT_EDGE",EDGE,{"disambiguationData":[OSD([sQuery(id+"F52.wireOp",EDGE,"E49.top"),sQuery(id+"F52.wireOp",EDGE,"E49.left")])]})});
            var Q5;
            Q5=makeQuery(id+"F53.boolean.opBoolean","COPY",EDGE,{"derivedFrom":makeQuery(id+"F53.opExtrude","SWEPT_EDGE",EDGE,{"disambiguationData":[OSD([sQuery(id+"F52.wireOp",EDGE,"E49.bottom"),sQuery(id+"F52.wireOp",EDGE,"E49.right")])]})});
            var Q6;
            Q6=makeQuery(id+"F53.boolean.opBoolean","COPY",EDGE,{"derivedFrom":makeQuery(id+"F53.opExtrude","SWEPT_EDGE",EDGE,{"disambiguationData":[OSD([sQuery(id+"F52.wireOp",EDGE,"E49.top"),sQuery(id+"F52.wireOp",EDGE,"E49.right")])]})});
            var Q7;
            Q7=makeQuery(id+"F55.boolean.opBoolean","COPY",EDGE,{"derivedFrom":makeQuery(id+"F55.opExtrude","SWEPT_EDGE",EDGE,{"disambiguationData":[OSD([sQuery(id+"F54.wireOp",EDGE,"E50.bottom"),sQuery(id+"F54.wireOp",EDGE,"E50.right")])]})});
            fillet(context, id + "F56", {"entities" : qUnion([Q0, Q1, Q2, Q3, Q4, Q5, Q6, Q7]), "radius" : 4.76 * mm, "tangentPropagation" : true, "allowEdgeOverflow" : false});
        }
        {
            var Q0;
            Q0=makeQuery(id+"F1.opExtrude","SWEPT_FACE",FACE,{"disambiguationData":[OSD([sQuery(id+"F0.wireOp",EDGE,"E0.left")])]});
            var sketch = newSketch(context, id + "F57", { "sketchPlane" : qUnion([Q0])});
            skText(sketch, "E51", { "text": "TR", "fontName": "AllertaStencil-Regular.ttf"});
            const initialGuessF57  = {"E51": [-0.0762, 0.20514, 1, 0, 0.0425]};
            skSetInitialGuess(sketch, initialGuessF57);
            skSolve(sketch);
        }
        {
            var Q0;
            Q0=qSketchRegion(id+"F57",true);
            extrude(context, id + "F58", {"entities" : qUnion([Q0]), "operationType" : NewBodyOperationType.REMOVE, "oppositeDirection" : true, "depth" : 4.76 * mm});
        }
        {
            var Q0;
            Q0=makeQuery(id+"F7.boolean.opBoolean","COPY",FACE,{"derivedFrom":makeQuery(id+"F7.opExtrude","SWEPT_FACE",FACE,{"disambiguationData":[OSD([sQuery(id+"F6.wireOp",EDGE,"E10")])]})});
            var sketch = newSketch(context, id + "F59", { "sketchPlane" : qUnion([Q0])});
            skCircle(sketch, "E52", {"center": v(-176.28, 114.88) * mm, "radius": 2.38 * mm});
            skPoint(sketch, "E52.centerSnap0", {"position": v(-171.51, 114.88) * mm});
            skCircle(sketch, "E53", {"center": v(-135, 114.88) * mm, "radius": 2.38 * mm});
            skPoint(sketch, "E53.centerSnap0", {"position": v(-139.76, 114.88) * mm});
            skSolve(sketch);
        }
        {
            var Q0;
            Q0=qSketchRegion(id+"F59",true);
            extrude(context, id + "F60", {"entities" : qUnion([Q0]), "operationType" : NewBodyOperationType.REMOVE, "oppositeDirection" : true, "depth" : 4.76 * mm});
        }
        {
            var Q0;
            Q0=makeQuery(id+"F7.boolean.opBoolean","COPY",FACE,{"derivedFrom":makeQuery(id+"F7.opExtrude","SWEPT_FACE",FACE,{"disambiguationData":[OSD([sQuery(id+"F6.wireOp",EDGE,"E12")])]})});
            var sketch = newSketch(context, id + "F61", { "sketchPlane" : qUnion([Q0])});
            skCircle(sketch, "E54", {"center": v(176.28, 114.88) * mm, "radius": 2.38 * mm});
            skPoint(sketch, "E54.centerSnap0", {"position": v(171.51, 114.88) * mm});
            skCircle(sketch, "E55", {"center": v(135, 114.88) * mm, "radius": 2.38 * mm});
            skPoint(sketch, "E55.centerSnap0", {"position": v(139.76, 114.88) * mm});
            skSolve(sketch);
        }
        {
            var Q0;
            Q0=qSketchRegion(id+"F61",true);
            extrude(context, id + "F62", {"entities" : qUnion([Q0]), "operationType" : NewBodyOperationType.REMOVE, "oppositeDirection" : true, "depth" : 4.76 * mm});
        }
        {
            var Q0;
            Q0=makeQuery(id+"F1.opExtrude","SWEPT_FACE",FACE,{"disambiguationData":[OSD([sQuery(id+"F0.wireOp",EDGE,"E0.left")])]});
            var sketch = newSketch(context, id + "F63", { "sketchPlane" : qUnion([Q0])});
            skLineSegment(sketch, "E56", {"start": v(95.25, 0) * mm, "end": v(-101.6, 25.4) * mm});
            skLineSegment(sketch, "E57", {"start": v(-101.6, 25.4) * mm, "end": v(-101.6, 0) * mm});
            skLineSegment(sketch, "E58", {"start": v(-101.6, 0) * mm, "end": v(95.25, 0) * mm});
            skSolve(sketch);
        }
        {
            var Q0;
            Q0=qSketchRegion(id+"F63",true);
            extrude(context, id + "F64", {"entities" : qUnion([Q0]), "operationType" : NewBodyOperationType.REMOVE, "endBound" : BoundingType.THROUGH_ALL, "oppositeDirection" : true, "depth" : 25.4 * mm, "offsetDistance" : 25.4 * mm});
        }
    });
